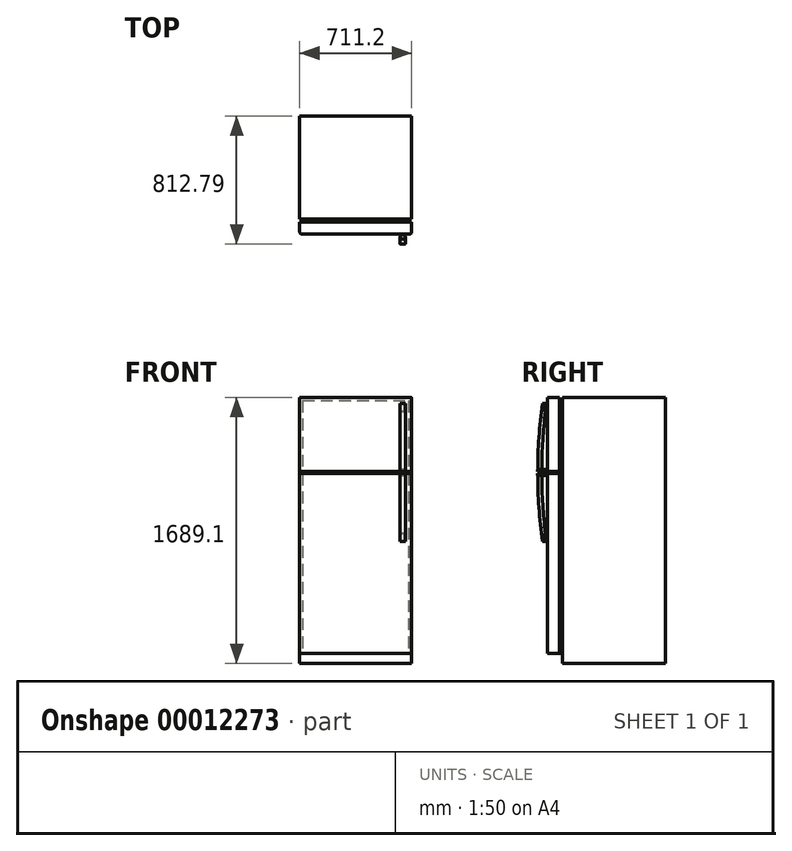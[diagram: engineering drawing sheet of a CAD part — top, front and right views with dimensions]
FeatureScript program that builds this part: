
annotation { "Feature Type Name" : "Feature", "Feature Type Description" : "" }
export const myFeature = defineFeature(function(context is Context, id is Id, definition is map)
    precondition{}
    {
        {
            var Q0;
            Q0=qCreatedBy(makeId("Front.planeOp"),FACE);
            cPlane(context, id + "F0", {"entities" : qUnion([Q0]), "cplaneType" : CPlaneType.OFFSET, "offset" : 654.05 * mm, "width" : 152.4 * mm, "height" : 152.4 * mm});
        }
        {
            var Q0;
            Q0=qCreatedBy(id+"F0.planeOp",FACE);
            cPlane(context, id + "F1", {"entities" : qUnion([Q0]), "cplaneType" : CPlaneType.OFFSET, "offset" : 95.25 * mm, "width" : 152.4 * mm, "height" : 152.4 * mm});
        }
        {
            var Q0;
            Q0=qCreatedBy(makeId("Right.planeOp"),FACE);
            cPlane(context, id + "F2", {"entities" : qUnion([Q0]), "cplaneType" : CPlaneType.OFFSET, "offset" : 298.45 * mm, "width" : 152.4 * mm, "height" : 152.4 * mm});
        }
        {
            var Q0;
            Q0=qCreatedBy(id+"F0.planeOp",FACE);
            var sketch = newSketch(context, id + "F3", { "sketchPlane" : qUnion([Q0])});
            skLineSegment(sketch, "E0.bottom", {"start": v(-355.6, 0) * mm, "end": v(355.6, 0) * mm});
            skLineSegment(sketch, "E0.top", {"start": v(-355.6, 1689.1) * mm, "end": v(355.6, 1689.1) * mm});
            skLineSegment(sketch, "E0.left", {"start": v(-355.6, 0) * mm, "end": v(-355.6, 1689.1) * mm});
            skLineSegment(sketch, "E0.right", {"start": v(355.6, 0) * mm, "end": v(355.6, 1689.1) * mm});
            skLineSegment(sketch, "E1", {"start": v(-355.6, 1219.2) * mm, "end": v(355.6, 1219.2) * mm});
            skLineSegment(sketch, "E2", {"start": v(-355.6, 1206.5) * mm, "end": v(355.6, 1206.5) * mm});
            skLineSegment(sketch, "E3", {"start": v(-355.6, 63.5) * mm, "end": v(355.6, 63.5) * mm});
            skLineSegment(sketch, "E4.bottom", {"start": v(-336.55, 1670.05) * mm, "end": v(336.55, 1670.05) * mm});
            skLineSegment(sketch, "E4.left", {"start": v(-336.55, 1670.05) * mm, "end": v(-336.55, 63.5) * mm});
            skLineSegment(sketch, "E4.right", {"start": v(336.55, 1670.05) * mm, "end": v(336.55, 63.5) * mm});
            skSolve(sketch);
        }
        {
            var Q0;
            Q0=qCreatedBy(id+"F0.planeOp",FACE);
            var sketch = newSketch(context, id + "F4", { "sketchPlane" : qUnion([Q0])});
            skLineSegment(sketch, "E5.bottom", {"start": v(-355.6, 1689.1) * mm, "end": v(355.6, 1689.1) * mm});
            skLineSegment(sketch, "E5.top", {"start": v(-355.6, 0) * mm, "end": v(355.6, 0) * mm});
            skLineSegment(sketch, "E5.left", {"start": v(-355.6, 1689.1) * mm, "end": v(-355.6, 0) * mm});
            skLineSegment(sketch, "E5.right", {"start": v(355.6, 1689.1) * mm, "end": v(355.6, 0) * mm});
            skSolve(sketch);
        }
        {
            var Q0;
            Q0 = qSketchRegion(id + "F4", true);
            var Q1;
            Q1=qCreatedBy(makeId("Front.planeOp"),FACE);
            var Q2;
            Q2=qCreatedBy(id+"F1.planeOp",FACE);
            extrude(context, id + "F5", {"entities" : qUnion([Q0]), "endBound" : BoundingType.UP_TO_SURFACE, "oppositeDirection" : true, "endBoundEntityFace" : qUnion([Q1]), "depth" : 25.4 * mm, "hasSecondDirection" : true, "secondDirectionBound" : BoundingType.UP_TO_SURFACE, "secondDirectionOppositeDirection" : false, "secondDirectionBoundEntityFace" : qUnion([Q2]), "secondDirectionDepth" : 44.45 * mm});
        }
        {
            var Q0;
            Q0=makeQuery(id+"F5.opExtrude","CAP_EDGE",EDGE,{"disambiguationData":[OSD([sQuery(id+"F4.wireOp",EDGE,"E5.left")])],"isStart":true});
            var Q1;
            Q1=makeQuery(id+"F5.opExtrude","CAP_EDGE",EDGE,{"disambiguationData":[OSD([sQuery(id+"F4.wireOp",EDGE,"E5.right")])],"isStart":true});
            fillet(context, id + "F6", {"entities" : qUnion([Q0, Q1]), "radius" : 12.7 * mm, "tangentPropagation" : true, "allowEdgeOverflow" : false});
        }
        {
            var Q0;
            Q0=qCreatedBy(id+"F2.planeOp",FACE);
            var sketch = newSketch(context, id + "F7", { "sketchPlane" : qUnion([Q0])});
            skArc(sketch, "E6", {"start": v(-781.05, 1651) * mm, "mid": v(-812.8, 1212.85) * mm, "end": v(-781.05, 774.7) * mm});
            skLineSegment(sketch, "E7", {"start": v(-654.05, 1689.1) * mm, "end": v(-805.03, 1689.1) * mm, "construction": true});
            skPoint(sketch, "E8", {"position": v(-812.8, 1212.85) * mm});
            skLineSegment(sketch, "E9", {"start": v(-781.05, 1651) * mm, "end": v(-755.65, 1651) * mm});
            skLineSegment(sketch, "E10", {"start": v(-781.05, 774.7) * mm, "end": v(-755.65, 774.7) * mm});
            skArc(sketch, "E11", {"start": v(-755.65, 1651) * mm, "mid": v(-787.4, 1212.85) * mm, "end": v(-755.65, 774.7) * mm});
            skSolve(sketch);
        }
        {
            var Q0;
            Q0=makeQuery(id+"F7.imprint","IMPRINT",FACE,{"disambiguationData":[TD([[makeQuery(id+"F7.imprint","IMPRINT",EDGE,{"derivedFrom":sQuery(id+"F7.wireOp",EDGE,"E6")}),1.0]])]});
            extrude(context, id + "F8", {"entities" : qUnion([Q0]), "depth" : 34.92 * mm, "symmetric" : true});
        }
        {
            var Q0;
            Q0=makeQuery(id+"F8.opExtrude","CAP_EDGE",EDGE,{"disambiguationData":[OSD([sQuery(id+"F7.wireOp",EDGE,"E11")])],"isStart":false});
            var Q1;
            Q1=makeQuery(id+"F8.opExtrude","CAP_EDGE",EDGE,{"disambiguationData":[OSD([sQuery(id+"F7.wireOp",EDGE,"E11")])],"isStart":true});
            fillet(context, id + "F9", {"entities" : qUnion([Q0, Q1]), "radius" : 16.5 * mm, "tangentPropagation" : true, "allowEdgeOverflow" : false});
        }
        {
            var Q0;
            Q0=qCreatedBy(id+"F1.planeOp",FACE);
            var sketch = newSketch(context, id + "F10", { "sketchPlane" : qUnion([Q0])});
            skLineSegment(sketch, "E12.bottom", {"start": v(285.75, 1651) * mm, "end": v(311.15, 1651) * mm});
            skLineSegment(sketch, "E12.top", {"start": v(285.75, 1600.2) * mm, "end": v(311.15, 1600.2) * mm});
            skLineSegment(sketch, "E12.left", {"start": v(285.75, 1651) * mm, "end": v(285.75, 1600.2) * mm});
            skLineSegment(sketch, "E12.right", {"start": v(311.15, 1651) * mm, "end": v(311.15, 1600.2) * mm});
            skLineSegment(sketch, "E13.bottom", {"start": v(285.75, 1231.9) * mm, "end": v(311.15, 1231.9) * mm});
            skLineSegment(sketch, "E13.top", {"start": v(285.75, 1219.2) * mm, "end": v(311.15, 1219.2) * mm});
            skLineSegment(sketch, "E13.left", {"start": v(285.75, 1231.9) * mm, "end": v(285.75, 1219.2) * mm});
            skLineSegment(sketch, "E13.right", {"start": v(311.15, 1231.9) * mm, "end": v(311.15, 1219.2) * mm});
            skLineSegment(sketch, "E14.bottom", {"start": v(285.75, 1206.5) * mm, "end": v(311.15, 1206.5) * mm});
            skLineSegment(sketch, "E14.top", {"start": v(285.75, 1193.8) * mm, "end": v(311.15, 1193.8) * mm});
            skLineSegment(sketch, "E14.left", {"start": v(285.75, 1206.5) * mm, "end": v(285.75, 1193.8) * mm});
            skLineSegment(sketch, "E14.right", {"start": v(311.15, 1206.5) * mm, "end": v(311.15, 1193.8) * mm});
            skLineSegment(sketch, "E15.bottom", {"start": v(285.75, 825.5) * mm, "end": v(311.15, 825.5) * mm});
            skLineSegment(sketch, "E15.top", {"start": v(285.75, 774.7) * mm, "end": v(311.15, 774.7) * mm});
            skLineSegment(sketch, "E15.left", {"start": v(285.75, 825.5) * mm, "end": v(285.75, 774.7) * mm});
            skLineSegment(sketch, "E15.right", {"start": v(311.15, 825.5) * mm, "end": v(311.15, 774.7) * mm});
            skPoint(sketch, "E16", {"position": v(298.45, 1651) * mm});
            skLineSegment(sketch, "E17.0", {"start": v(-355.6, 1219.2) * mm, "end": v(355.6, 1219.2) * mm, "construction": true});
            skLineSegment(sketch, "E18.0", {"start": v(-355.6, 1206.5) * mm, "end": v(355.6, 1206.5) * mm, "construction": true});
            skLineSegment(sketch, "E19.0", {"start": v(298.45, 1651) * mm, "end": v(298.45, 774.7) * mm, "construction": true});
            skSolve(sketch);
        }
        {
            var Q0;
            Q0 = qSketchRegion(id + "F10", true);
            extrude(context, id + "F11", {"entities" : qUnion([Q0]), "operationType" : NewBodyOperationType.ADD, "endBound" : BoundingType.UP_TO_NEXT, "depth" : 25.4 * mm});
        }
        {
            var Q0;
            {var subQ10=sQuery(id+"F3.wireOp",EDGE,"E0.top");Q0=makeQuery(id+"F3.imprint","IMPRINT",FACE,{"disambiguationData":[TD([[makeQuery(id+"F3.imprint","IMPRINT",EDGE,{"derivedFrom":subQ10}),-1.0]])]});}
            var Q1;
            {var subQ3=sQuery(id+"F3.wireOp",EDGE,"E1");var subQ5=sQuery(id+"F3.wireOp",EDGE,"E0.right");var subQ6=makeQuery(id+"F3.imprint","INTERSECT",VERTEX,{"derivedFrom":[subQ5,subQ3]});Q1=makeQuery(id+"F3.imprint","IMPRINT",FACE,{"disambiguationData":[TD([[makeQuery(id+"F3.imprint","IMPRINT",EDGE,{"disambiguationData":[TD([[subQ6,1.0]])],"derivedFrom":subQ5}),1.0]])]});}
            var Q2;
            {var subQ1=sQuery(id+"F3.wireOp",EDGE,"E2");var subQ5=sQuery(id+"F3.wireOp",EDGE,"E0.right");var subQ7=makeQuery(id+"F3.imprint","INTERSECT",VERTEX,{"derivedFrom":[subQ5,subQ1]});Q2=makeQuery(id+"F3.imprint","IMPRINT",FACE,{"disambiguationData":[TD([[makeQuery(id+"F3.imprint","IMPRINT",EDGE,{"disambiguationData":[TD([[subQ7,1.0]])],"derivedFrom":subQ5}),1.0]])]});}
            var Q3;
            {var subQ3=sQuery(id+"F3.wireOp",EDGE,"E1");var subQ5=sQuery(id+"F3.wireOp",EDGE,"E0.left");var subQ7=makeQuery(id+"F3.imprint","INTERSECT",VERTEX,{"derivedFrom":[subQ5,subQ3]});Q3=makeQuery(id+"F3.imprint","IMPRINT",FACE,{"disambiguationData":[TD([[makeQuery(id+"F3.imprint","IMPRINT",EDGE,{"disambiguationData":[TD([[subQ7,1.0]])],"derivedFrom":subQ5}),-1.0]])]});}
            var Q4;
            {var subQ1=sQuery(id+"F3.wireOp",EDGE,"E2");var subQ5=sQuery(id+"F3.wireOp",EDGE,"E0.left");var subQ7=makeQuery(id+"F3.imprint","INTERSECT",VERTEX,{"derivedFrom":[subQ5,subQ1]});Q4=makeQuery(id+"F3.imprint","IMPRINT",FACE,{"disambiguationData":[TD([[makeQuery(id+"F3.imprint","IMPRINT",EDGE,{"disambiguationData":[TD([[subQ7,1.0]])],"derivedFrom":subQ5}),-1.0]])]});}
            extrude(context, id + "F12", {"entities" : qUnion([Q0, Q1, Q2, Q3, Q4]), "operationType" : NewBodyOperationType.REMOVE, "depth" : 19.05 * mm});
        }
        {
            var Q0;
            {var subQ3=sQuery(id+"F3.wireOp",EDGE,"E1");var subQ5=sQuery(id+"F3.wireOp",EDGE,"E0.right");var subQ6=makeQuery(id+"F3.imprint","INTERSECT",VERTEX,{"derivedFrom":[subQ5,subQ3]});Q0=makeQuery(id+"F3.imprint","IMPRINT",FACE,{"disambiguationData":[TD([[makeQuery(id+"F3.imprint","IMPRINT",EDGE,{"disambiguationData":[TD([[subQ6,1.0]])],"derivedFrom":subQ5}),1.0]])]});}
            var Q1;
            {var subQ3=sQuery(id+"F3.wireOp",EDGE,"E1");var subQ5=sQuery(id+"F3.wireOp",EDGE,"E4.left");var subQ7=makeQuery(id+"F3.imprint","INTERSECT",VERTEX,{"derivedFrom":[subQ3,subQ5]});Q1=makeQuery(id+"F3.imprint","IMPRINT",FACE,{"disambiguationData":[TD([[makeQuery(id+"F3.imprint","IMPRINT",EDGE,{"disambiguationData":[TD([[subQ7,-1.0]])],"derivedFrom":subQ3}),-1.0]])]});}
            var Q2;
            {var subQ3=sQuery(id+"F3.wireOp",EDGE,"E1");var subQ5=sQuery(id+"F3.wireOp",EDGE,"E0.left");var subQ7=makeQuery(id+"F3.imprint","INTERSECT",VERTEX,{"derivedFrom":[subQ5,subQ3]});Q2=makeQuery(id+"F3.imprint","IMPRINT",FACE,{"disambiguationData":[TD([[makeQuery(id+"F3.imprint","IMPRINT",EDGE,{"disambiguationData":[TD([[subQ7,1.0]])],"derivedFrom":subQ5}),-1.0]])]});}
            var Q3;
            {var subQ7=sQuery(id+"F3.wireOp",EDGE,"E0.bottom");Q3=makeQuery(id+"F3.imprint","IMPRINT",FACE,{"disambiguationData":[TD([[makeQuery(id+"F3.imprint","IMPRINT",EDGE,{"derivedFrom":subQ7}),1.0]])]});}
            extrude(context, id + "F13", {"entities" : qUnion([Q0, Q1, Q2, Q3]), "operationType" : NewBodyOperationType.REMOVE, "endBound" : BoundingType.THROUGH_ALL, "depth" : 25.4 * mm});
        }
    });
